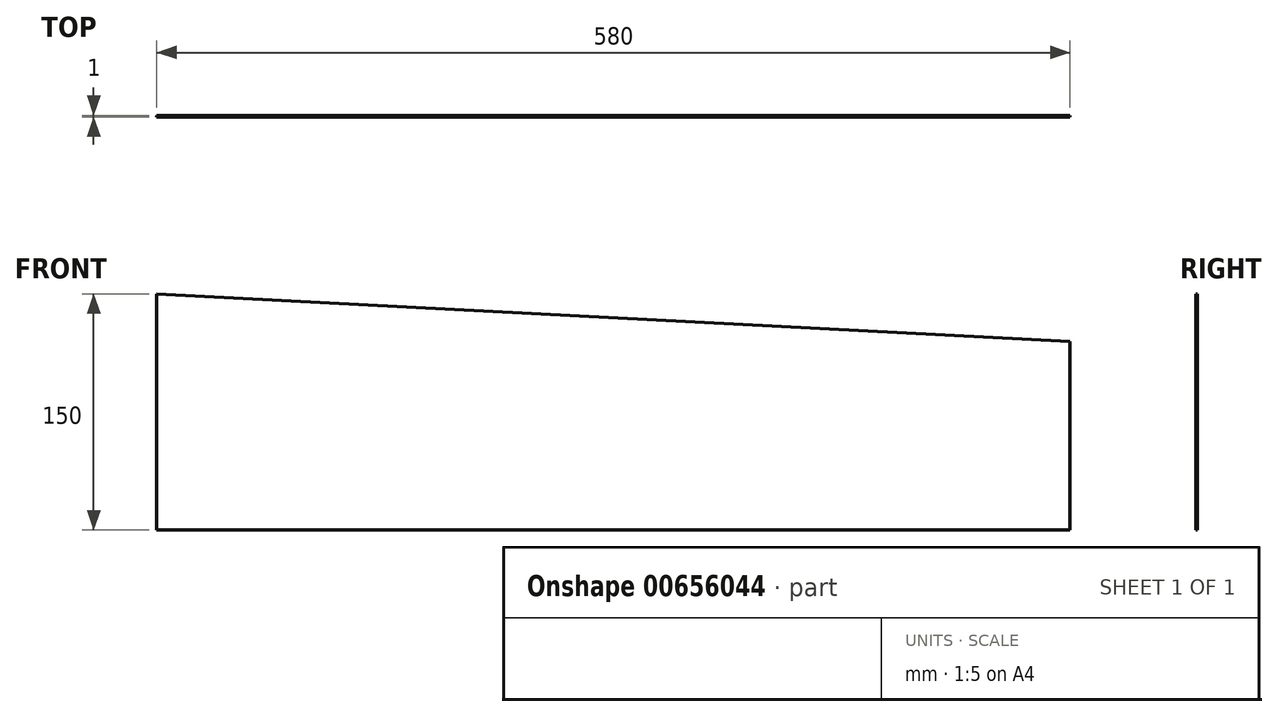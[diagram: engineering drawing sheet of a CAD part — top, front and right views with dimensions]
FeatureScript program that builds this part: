
annotation { "Feature Type Name" : "Feature", "Feature Type Description" : "" }
export const myFeature = defineFeature(function(context is Context, id is Id, definition is map)
    precondition{}
    {
        {
            var Q0;
            Q0=qCreatedBy(makeId("Front.planeOp"),FACE);
            var sketch = newSketch(context, id + "F0", { "sketchPlane" : qUnion([Q0])});
            skLineSegment(sketch, "E0", {"start": v(0, 0) * mm, "end": v(0, 150) * mm});
            skLineSegment(sketch, "E1", {"start": v(0, 150) * mm, "end": v(580, 120) * mm});
            skLineSegment(sketch, "E2", {"start": v(580, 120) * mm, "end": v(580, 0) * mm});
            skLineSegment(sketch, "E3", {"start": v(580, 0) * mm, "end": v(0, 0) * mm});
            skSolve(sketch);
        }
        {
            var Q0;
            Q0=makeQuery(id+"F0.imprint","IMPRINT",FACE,{"disambiguationData":[TD([[makeQuery(id+"F0.imprint","IMPRINT",EDGE,{"derivedFrom":sQuery(id+"F0.wireOp",EDGE,"E0")}),-1.0]])]});
            extrude(context, id + "F1", {"entities" : qUnion([Q0]), "depth" : 1 * mm, "offsetDistance" : 25.4 * mm});
        }
    });
